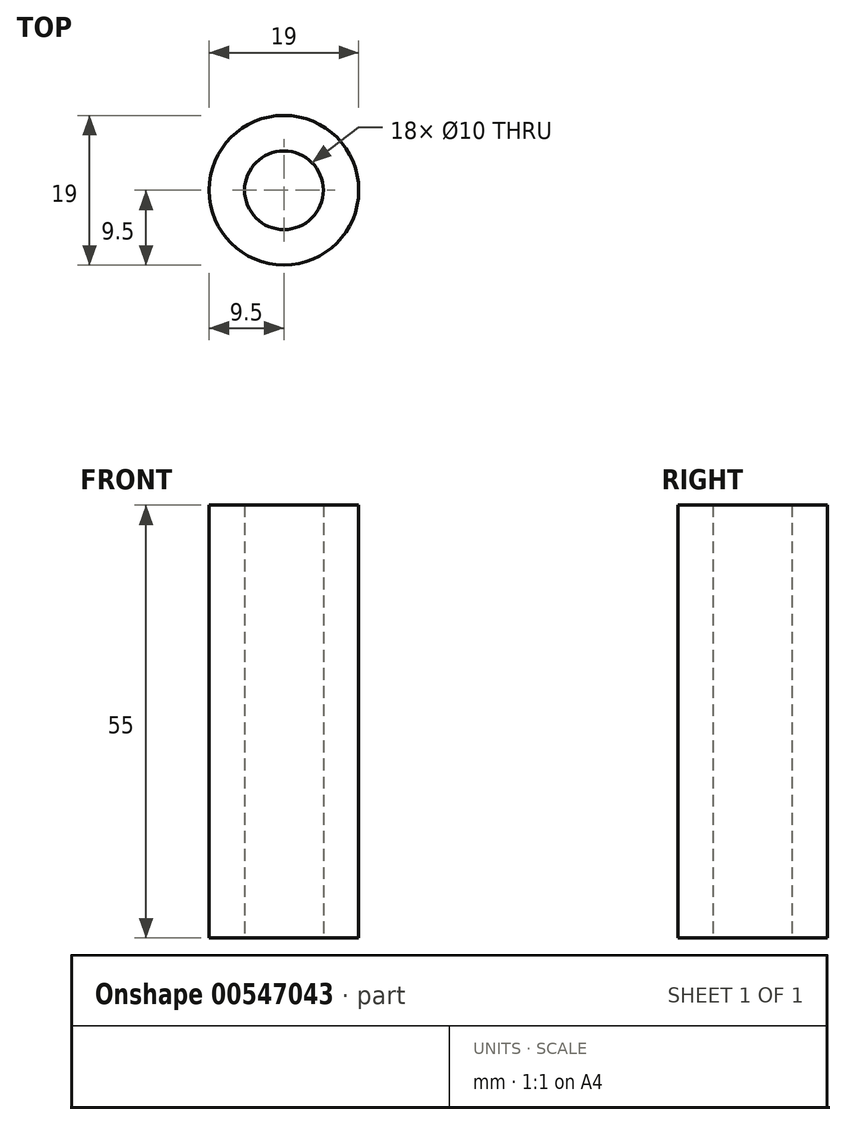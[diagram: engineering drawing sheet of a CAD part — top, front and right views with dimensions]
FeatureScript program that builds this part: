
annotation { "Feature Type Name" : "Feature", "Feature Type Description" : "" }
export const myFeature = defineFeature(function(context is Context, id is Id, definition is map)
    precondition{}
    {
        {
            var Q0;
            Q0=qCreatedBy(makeId("Top.planeOp"),FACE);
            var sketch = newSketch(context, id + "F0", { "sketchPlane" : qUnion([Q0])});
            skCircle(sketch, "E0", {"center": v(0, 0) * mm, "radius": 5 * mm});
            skCircle(sketch, "E1", {"center": v(0, 0) * mm, "radius": 9.5 * mm});
            skSolve(sketch);
        }
        {
            var Q0;
            Q0=makeQuery(id+"F0.imprint","IMPRINT",FACE,{"disambiguationData":[TD([[makeQuery(id+"F0.imprint","IMPRINT",EDGE,{"derivedFrom":sQuery(id+"F0.wireOp",EDGE,"E0")}),-1.0]])]});
            extrude(context, id + "F1", {"entities" : qUnion([Q0]), "depth" : 55 * mm, "offsetDistance" : 25 * mm});
        }
    });
